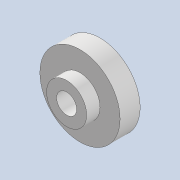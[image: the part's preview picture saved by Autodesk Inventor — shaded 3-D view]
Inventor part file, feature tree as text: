
AUTODESK INVENTOR PART (.ipt)
format: ipt  version: 2020 (Build 240168000, 168)  size: 165,888 bytes
history: native  units: mm
features: extrude x4, sketch x4, other x3, fillet x2, thicken_offset x1, plane x1, chamfer x1, reference x1
ambient origin geometry x8: Origin, YZ Plane, XZ Plane, XY Plane, X Axis, Y Axis, Z Axis, Center Point
bodies: Solid1 (feature_tree)
feature tree (17):
  extrude  "Extrusion1"  Depth=6.0mm
  extrude  "Extrusion2"  Depth=2.0mm
  extrude  "Extrusion3"  Depth=3.0mm
  thicken_offset  "Thicken1"
  plane  "Work Plane1"
  extrude  "Extrusion4"  Depth=2.0mm TaperAngle=0.0deg
  fillet  "Fillet1"  Radius=2.0mm
  chamfer  "Chamfer1"  Distance=2.0mm
  fillet  "Fillet2"  [1 undecoded]
  sketch  "Sketch1"  dims[d0=3.0mm d1=6.0mm]
  sketch  "Sketch2"  dims[d2=2.0mm d3=0.0mm d4=12.0mm]
  sketch  "Sketch3"  dims[d5=3.0mm d6=0.0mm d7=3.0mm]
  reference  "Reference1"
  sketch  "Sketch4"  dims[d8=6.0mm d9=2.0mm d10=0.0mm d11=2.0mm d12=2.0mm d13=-1.5mm d14=0.7mm d15=1.4mm d16=0.0mm d17=0.4mm d18=0.5mm d19=2.0mm d20=45.0deg d21=1.0mm]
  parser-record x1  (decoder bookkeeping rows leaked as tree rows — omitted from the tree; the rows remain in map.json)
  other  "tip_3_n_ass.iam"
  other  "pin3_40:2"
note: 1 required parameter value undecoded (feature->parameter linkage not recoverable at this tier; creation-order binding heuristic only, values carry confidence <= 0.55)
note: 1 file-system path scrubbed to <path> (originals preserved in map.json)
